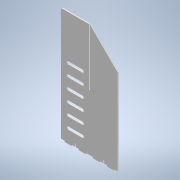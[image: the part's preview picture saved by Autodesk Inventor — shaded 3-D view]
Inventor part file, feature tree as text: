
AUTODESK INVENTOR PART (.ipt)
format: ipt  version: 2021.1 (Build 251245010, 245A)  size: 225,792 bytes
history: native  units: mm
features: other x4, extrude x2, sketch x2, reference x2
ambient origin geometry x8: Origin, YZ Plane, XZ Plane, XY Plane, X Axis, Y Axis, Z Axis, Center Point
bodies: Body1 (feature_tree)
feature tree (10):
  other  "Твердое тело1"
  extrude  "Корпус"  Depth=6.0mm
  extrude  "Пазы"  Depth=300.0mm
  sketch  "Эскиз1"
  sketch  "Эскиз2"
  reference  "Ссылка1"
  reference  "Ссылка2"
  other  "<userpath>\Documents\Savka\3d\Korp.iam"
  other  "Korp.iam"
  other  "Korpus 2:1"
